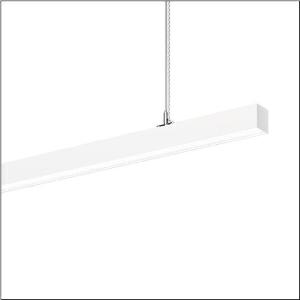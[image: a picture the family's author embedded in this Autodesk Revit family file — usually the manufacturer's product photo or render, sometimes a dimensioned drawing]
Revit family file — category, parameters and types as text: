
# Revit family: silica_r__21_51mx33da37wb_a2a9
name_source: partatom
category: Lighting Fixtures
units: mm (PartAtom-declared; Revit-internal decimal feet)

## family parameters
Cut with Voids When Loaded = No
Host = Face
Light Source = No
Part Type = Normal
Room Calculation Point = No
Round Connector Dimension = Use Diameter
Shared = No

## types (1)
- --- (1 x LED, 5910 lm, 41.3 W, 3000K)
    Apparent Load = 41 VA
    CIE Flux Codes = 78 96 99 55 100
    Color Rendering = 80
    Color Temperature = 3000K
    Default Elevation = 1800 mm
    Description = Silica® 21, office luminaire, primary optical cover: prismatic diffuser, of PMMA, CAT 2 (L<= 3000cd/m²), light emission: direct/indirect distribution, primary light characteristic: symmetric, installation type: suspended mounting, LED, rated luminous flux: 5.910lm, luminous efficacy: 143lm/W, light colour: 830, colour temperature: 3000K, with terminal, 3+2-pole, max. 2.5mm², mains connection: 220..240V, AC, 50/60Hz, rated input power: 41.3W, luminaire housing, of aluminium, traffic white (RAL 9016), length: 1.204mm, width: 53mm, height: 53mm, protection rating (complete): IP20, insulation class (complete): insulation class I (protective earthing), certification: CE, permissible operating ambient temperature: 0..+35°C, standard: EN 50419, packaging unit: 1 piece
    Height = 53 mm
    Lamp = 1 x LED
    Lamp Light Flux = 5910 lm
    Lamp Power = 41.3 W
    Lamp count = 1
    Length = 1204 mm
    Luminous efficacy = 143 lm/W
    Manufacturer = Siteco
    ModVariant = No
    Model = 51MX33DA37WB
    Mounting Place = Ceiling
    Mounting Type = Pendant
    Number of Poles = 1
    OnlyDefault = Yes
    Power Factor = 1
    Product Name = Silica® 21
    Product group = office luminaire | ceiling pendant
    ProductGroupID = 902
    Protection Class = Protection class I
    Protection Degree = IP 20
    RLX_Detail_Level = 1
    RLX_Emergency_Light_Flux = 0 lm
    RLX_Emergency_Type = 0
    RLX_Emergency_Type_DB = No
    RlxData = <blob elided: 21377 chars, md5=3ab4010d>
    Socket = socket
    Standby Power = 0 W
    System Light Flux = 5910 lm
    System Power = 41 W
    Type Comments = factory setting: luminous flux: 100 % | dim-lin: 254 | 345 mA
    Type Image = l_1335916.jpg
    URL = http://relux.com
    VarID = @adj_088045
    Voltage = 0 V
    Weight = 0.00 kg
    Width = 53 mm

## geometry (parser evidence)
native form markers: Blend x4, Sweep x15
no freeform markers — native parametric forms only
